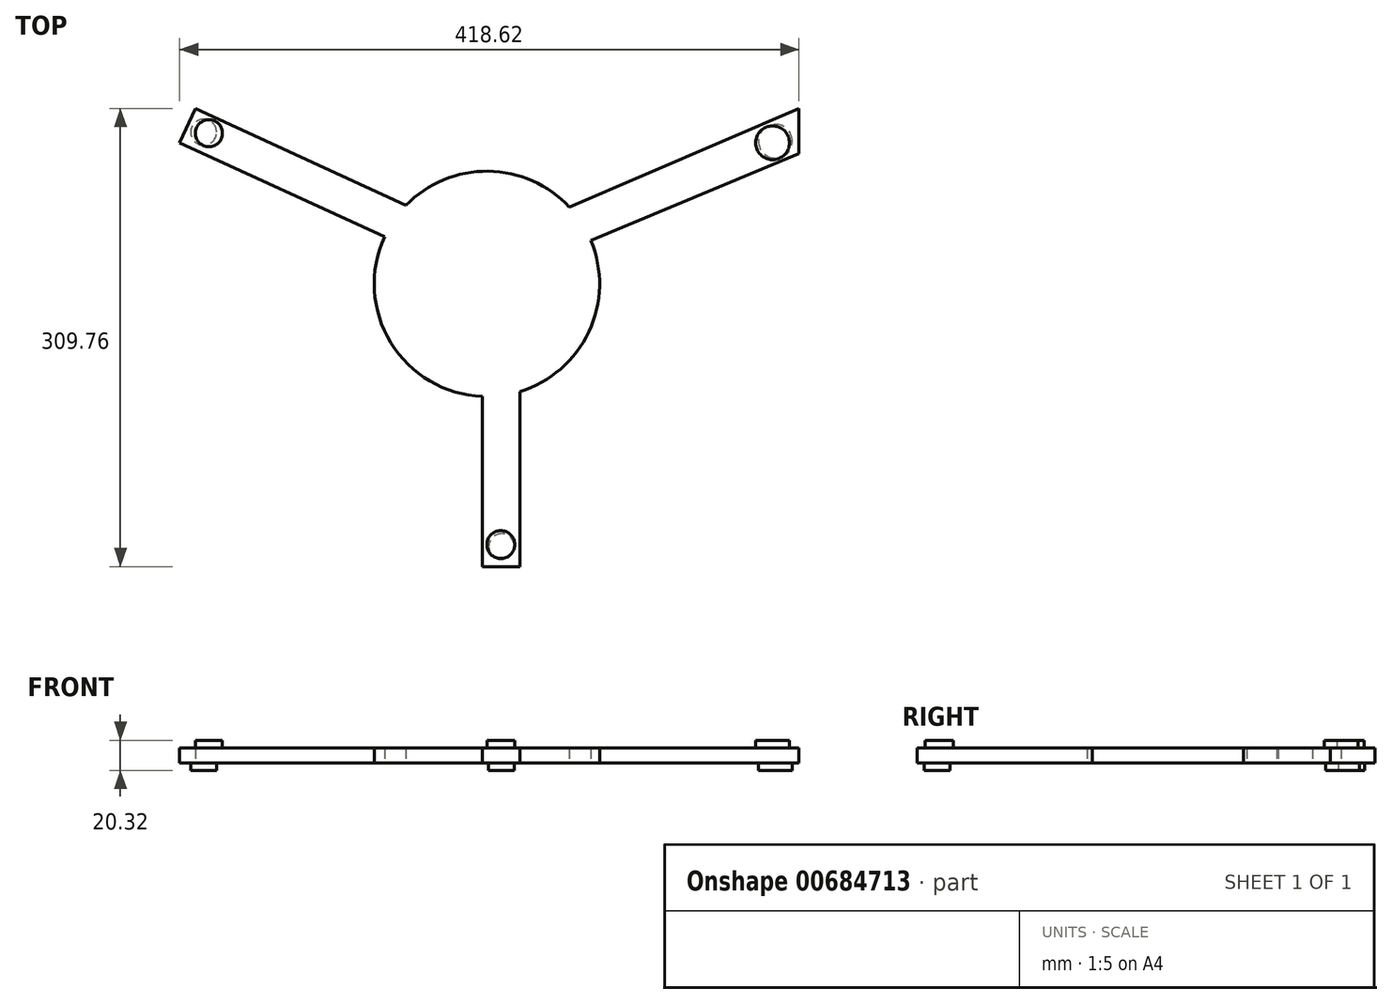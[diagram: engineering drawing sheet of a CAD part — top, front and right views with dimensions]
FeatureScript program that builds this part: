
annotation { "Feature Type Name" : "Feature", "Feature Type Description" : "" }
export const myFeature = defineFeature(function(context is Context, id is Id, definition is map)
    precondition{}
    {
        {
            var Q0;
            Q0=qCreatedBy(makeId("Top.planeOp"),FACE);
            var sketch = newSketch(context, id + "F0", { "sketchPlane" : qUnion([Q0])});
            skCircle(sketch, "E0", {"center": v(0, 0) * mm, "radius": 76.2 * mm});
            skLineSegment(sketch, "E1", {"start": v(0, 0) * mm, "end": v(-207.72, 95.44) * mm});
            skLineSegment(sketch, "E2", {"start": v(0, 27.95) * mm, "end": v(-197.12, 118.52) * mm});
            skLineSegment(sketch, "E3", {"start": v(-207.72, 95.44) * mm, "end": v(-197.12, 118.52) * mm});
            skLineSegment(sketch, "E4", {"start": v(0, 27.95) * mm, "end": v(210.9, 118.52) * mm});
            skLineSegment(sketch, "E5", {"start": v(0, 0) * mm, "end": v(210.9, 88.2) * mm});
            skLineSegment(sketch, "E6", {"start": v(210.9, 118.52) * mm, "end": v(210.9, 88.2) * mm});
            skLineSegment(sketch, "E7.bottom", {"start": v(-3.06, 37.36) * mm, "end": v(22.34, 37.36) * mm});
            skLineSegment(sketch, "E7.top", {"start": v(-3.06, -191.24) * mm, "end": v(22.34, -191.24) * mm});
            skLineSegment(sketch, "E7.left", {"start": v(-3.06, 37.36) * mm, "end": v(-3.06, -191.24) * mm});
            skLineSegment(sketch, "E7.right", {"start": v(22.34, 37.36) * mm, "end": v(22.34, -191.24) * mm});
            skSolve(sketch);
        }
        {
            var Q0;
            Q0=qCreatedBy(makeId("Top.planeOp"),FACE);
            var sketch = newSketch(context, id + "F1", { "sketchPlane" : qUnion([Q0])});
            skCircle(sketch, "E8", {"center": v(-187.97, 101.89) * mm, "radius": 9.15 * mm});
            skCircle(sketch, "E9", {"center": v(9.43, -176.32) * mm, "radius": 9.43 * mm});
            skCircle(sketch, "E10", {"center": v(193.2, 95.4) * mm, "radius": 11.44 * mm});
            skSolve(sketch);
        }
        {
            var Q0;
            Q0 = qSketchRegion(id + "F0", true);
            var Q1;
            {var subQ6=sQuery(id+"F0.wireOp",EDGE,"E1");var subQ9=sQuery(id+"F0.wireOp",EDGE,"E5");var subQ10=makeQuery(id+"F0.imprint","INTERSECT",VERTEX,{"derivedFrom":[subQ6,subQ9]});Q1=makeQuery(id+"F0.imprint","IMPRINT",FACE,{"disambiguationData":[TD([[makeQuery(id+"F0.imprint","IMPRINT",EDGE,{"disambiguationData":[TD([[subQ10,-1.0]])],"derivedFrom":subQ6}),-1.0]])]});}
            var Q2;
            {var subQ0=sQuery(id+"F0.wireOp",EDGE,"E4");var subQ1=sQuery(id+"F0.wireOp",EDGE,"E2");var subQ2=makeQuery(id+"F0.imprint","INTERSECT",VERTEX,{"derivedFrom":[subQ1,subQ0]});Q2=makeQuery(id+"F0.imprint","IMPRINT",FACE,{"disambiguationData":[TD([[makeQuery(id+"F0.imprint","IMPRINT",EDGE,{"disambiguationData":[TD([[subQ2,-1.0]])],"derivedFrom":subQ1}),-1.0]])]});}
            extrude(context, id + "F2", {"entities" : qUnion([Q0, Q1, Q2]), "depth" : 10.16 * mm, "offsetDistance" : 25.4 * mm});
        }
        {
            var Q0;
            Q0 = qSketchRegion(id + "F1", true);
            extrude(context, id + "F3", {"entities" : qUnion([Q0]), "operationType" : NewBodyOperationType.ADD, "depth" : 15.24 * mm, "offsetDistance" : 25.4 * mm});
        }
        {
            var Q0;
            Q0=qCreatedBy(makeId("Top.planeOp"),FACE);
            var sketch = newSketch(context, id + "F4", { "sketchPlane" : qUnion([Q0])});
            skCircle(sketch, "E11", {"center": v(9.94, -177.68) * mm, "radius": 8.74 * mm});
            skCircle(sketch, "E12", {"center": v(195.07, 96.43) * mm, "radius": 11.44 * mm});
            skCircle(sketch, "E13", {"center": v(-191.55, 102.57) * mm, "radius": 8.74 * mm});
            skSolve(sketch);
        }
        {
            var Q0;
            Q0=makeQuery(id+"F4.imprint","IMPRINT",FACE,{"disambiguationData":[TD([[makeQuery(id+"F4.imprint","IMPRINT",EDGE,{"derivedFrom":sQuery(id+"F4.wireOp",EDGE,"E11")}),1.0]])]});
            var Q1;
            Q1=makeQuery(id+"F4.imprint","IMPRINT",FACE,{"disambiguationData":[TD([[makeQuery(id+"F4.imprint","IMPRINT",EDGE,{"derivedFrom":sQuery(id+"F4.wireOp",EDGE,"E13")}),1.0]])]});
            var Q2;
            Q2=makeQuery(id+"F4.imprint","IMPRINT",FACE,{"disambiguationData":[TD([[makeQuery(id+"F4.imprint","IMPRINT",EDGE,{"derivedFrom":sQuery(id+"F4.wireOp",EDGE,"E12")}),1.0]])]});
            extrude(context, id + "F5", {"entities" : qUnion([Q0, Q1, Q2]), "operationType" : NewBodyOperationType.ADD, "oppositeDirection" : true, "depth" : 5.08 * mm, "offsetDistance" : 25.4 * mm});
        }
    });
